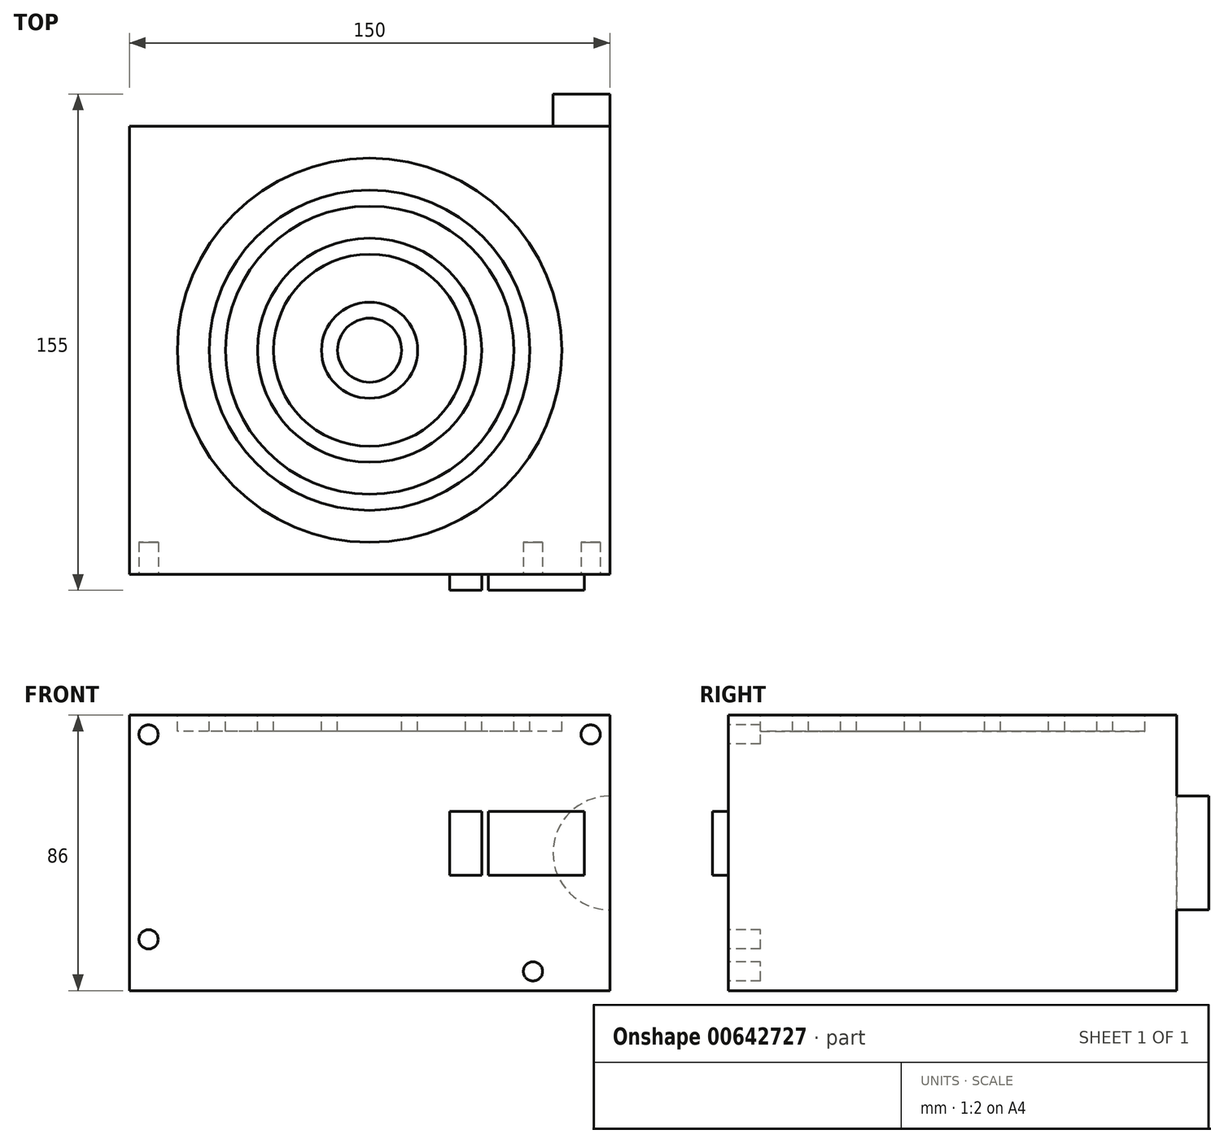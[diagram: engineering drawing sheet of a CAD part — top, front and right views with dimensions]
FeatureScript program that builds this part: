
annotation { "Feature Type Name" : "Feature", "Feature Type Description" : "" }
export const myFeature = defineFeature(function(context is Context, id is Id, definition is map)
    precondition{}
    {
        {
            var Q0;
            Q0=qCreatedBy(makeId("Top.planeOp"),FACE);
            var sketch = newSketch(context, id + "F0", { "sketchPlane" : qUnion([Q0])});
            skLineSegment(sketch, "E0.bottom", {"start": v(-67.65, 94.12) * mm, "end": v(82.35, 94.12) * mm});
            skLineSegment(sketch, "E0.top", {"start": v(-67.65, -45.88) * mm, "end": v(82.35, -45.88) * mm});
            skLineSegment(sketch, "E0.left", {"start": v(-67.65, 94.12) * mm, "end": v(-67.65, -45.88) * mm});
            skLineSegment(sketch, "E0.right", {"start": v(82.35, 94.12) * mm, "end": v(82.35, -45.88) * mm});
            skSolve(sketch);
        }
        {
            var Q0;
            Q0=makeQuery(id+"F0.imprint","IMPRINT",FACE,{"disambiguationData":[TD([[makeQuery(id+"F0.imprint","IMPRINT",EDGE,{"derivedFrom":sQuery(id+"F0.wireOp",EDGE,"E0.bottom")}),-1.0]])]});
            extrude(context, id + "F1", {"entities" : qUnion([Q0]), "depth" : 86 * mm, "offsetDistance" : 25 * mm});
        }
        {
            var Q0;
            Q0=makeQuery(id+"F1.opExtrude","SWEPT_FACE",FACE,{"disambiguationData":[OSD([sQuery(id+"F0.wireOp",EDGE,"E0.top")])]});
            var sketch = newSketch(context, id + "F2", { "sketchPlane" : qUnion([Q0])});
            skCircle(sketch, "E1", {"center": v(-61.65, 80) * mm, "radius": 3 * mm});
            skCircle(sketch, "E2", {"center": v(-61.65, 16) * mm, "radius": 3 * mm});
            skCircle(sketch, "E3", {"center": v(76.35, 80) * mm, "radius": 3 * mm});
            skCircle(sketch, "E4", {"center": v(58.35, 6) * mm, "radius": 3 * mm});
            skLineSegment(sketch, "E5.bottom", {"start": v(44.35, 56) * mm, "end": v(74.35, 56) * mm});
            skLineSegment(sketch, "E5.top", {"start": v(44.35, 36) * mm, "end": v(74.35, 36) * mm});
            skLineSegment(sketch, "E5.left", {"start": v(44.35, 56) * mm, "end": v(44.35, 36) * mm});
            skLineSegment(sketch, "E5.right", {"start": v(74.35, 56) * mm, "end": v(74.35, 36) * mm});
            skLineSegment(sketch, "E6.bottom", {"start": v(32.35, 56) * mm, "end": v(42.35, 56) * mm});
            skLineSegment(sketch, "E6.top", {"start": v(32.35, 36) * mm, "end": v(42.35, 36) * mm});
            skLineSegment(sketch, "E6.left", {"start": v(32.35, 56) * mm, "end": v(32.35, 36) * mm});
            skLineSegment(sketch, "E6.right", {"start": v(42.35, 56) * mm, "end": v(42.35, 36) * mm});
            skSolve(sketch);
        }
        {
            var Q0;
            Q0=makeQuery(id+"F2.imprint","IMPRINT",FACE,{"disambiguationData":[TD([[makeQuery(id+"F2.imprint","IMPRINT",EDGE,{"derivedFrom":sQuery(id+"F2.wireOp",EDGE,"E1")}),1.0]])]});
            var Q1;
            Q1=makeQuery(id+"F2.imprint","IMPRINT",FACE,{"disambiguationData":[TD([[makeQuery(id+"F2.imprint","IMPRINT",EDGE,{"derivedFrom":sQuery(id+"F2.wireOp",EDGE,"E2")}),1.0]])]});
            var Q2;
            Q2=makeQuery(id+"F2.imprint","IMPRINT",FACE,{"disambiguationData":[TD([[makeQuery(id+"F2.imprint","IMPRINT",EDGE,{"derivedFrom":sQuery(id+"F2.wireOp",EDGE,"E3")}),1.0]])]});
            var Q3;
            Q3=makeQuery(id+"F2.imprint","IMPRINT",FACE,{"disambiguationData":[TD([[makeQuery(id+"F2.imprint","IMPRINT",EDGE,{"derivedFrom":sQuery(id+"F2.wireOp",EDGE,"E4")}),1.0]])]});
            extrude(context, id + "F3", {"entities" : qUnion([Q0, Q1, Q2, Q3]), "operationType" : NewBodyOperationType.REMOVE, "oppositeDirection" : true, "depth" : 10 * mm, "offsetDistance" : 25 * mm});
        }
        {
            var Q0;
            Q0=makeQuery(id+"F2.imprint","IMPRINT",FACE,{"disambiguationData":[TD([[makeQuery(id+"F2.imprint","IMPRINT",EDGE,{"derivedFrom":sQuery(id+"F2.wireOp",EDGE,"E5.bottom")}),-1.0]])]});
            var Q1;
            Q1=makeQuery(id+"F2.imprint","IMPRINT",FACE,{"disambiguationData":[TD([[makeQuery(id+"F2.imprint","IMPRINT",EDGE,{"derivedFrom":sQuery(id+"F2.wireOp",EDGE,"E6.bottom")}),-1.0]])]});
            extrude(context, id + "F4", {"entities" : qUnion([Q0, Q1]), "operationType" : NewBodyOperationType.ADD, "depth" : 5 * mm, "offsetDistance" : 25 * mm});
        }
        {
            var Q0;
            Q0=makeQuery(id+"F1.opExtrude","CAP_FACE",FACE,{"disambiguationData":[OSD([sQuery(id+"F0.wireOp",EDGE,"E0.bottom"),sQuery(id+"F0.wireOp",EDGE,"E0.top"),sQuery(id+"F0.wireOp",EDGE,"E0.left"),sQuery(id+"F0.wireOp",EDGE,"E0.right")])],"isStart":false});
            var sketch = newSketch(context, id + "F5", { "sketchPlane" : qUnion([Q0])});
            skCircle(sketch, "E7", {"center": v(7.35, 24.12) * mm, "radius": 60 * mm});
            skPoint(sketch, "E7.centerSnap0", {"position": v(7.35, 94.12) * mm});
            skPoint(sketch, "E7.centerSnap1", {"position": v(82.35, 24.12) * mm});
            skCircle(sketch, "E8.0", {"center": v(7.35, 24.12) * mm, "radius": 50 * mm});
            skCircle(sketch, "E9.0", {"center": v(7.35, 24.12) * mm, "radius": 45 * mm});
            skCircle(sketch, "E10.0", {"center": v(7.35, 24.12) * mm, "radius": 35 * mm});
            skCircle(sketch, "E11.0", {"center": v(7.35, 24.12) * mm, "radius": 30 * mm});
            skCircle(sketch, "E12.0", {"center": v(7.35, 24.12) * mm, "radius": 15 * mm});
            skCircle(sketch, "E13.0", {"center": v(7.35, 24.12) * mm, "radius": 10 * mm});
            skSolve(sketch);
        }
        {
            var Q0;
            Q0=makeQuery(id+"F5.imprint","IMPRINT",FACE,{"disambiguationData":[TD([[makeQuery(id+"F5.imprint","IMPRINT",EDGE,{"derivedFrom":sQuery(id+"F5.wireOp",EDGE,"E7")}),1.0]])]});
            var Q1;
            Q1=makeQuery(id+"F5.imprint","IMPRINT",FACE,{"disambiguationData":[TD([[makeQuery(id+"F5.imprint","IMPRINT",EDGE,{"derivedFrom":sQuery(id+"F5.wireOp",EDGE,"E9.0")}),1.0]])]});
            var Q2;
            Q2=makeQuery(id+"F5.imprint","IMPRINT",FACE,{"disambiguationData":[TD([[makeQuery(id+"F5.imprint","IMPRINT",EDGE,{"derivedFrom":sQuery(id+"F5.wireOp",EDGE,"E11.0")}),1.0]])]});
            var Q3;
            Q3=makeQuery(id+"F5.imprint","IMPRINT",FACE,{"disambiguationData":[TD([[makeQuery(id+"F5.imprint","IMPRINT",EDGE,{"derivedFrom":sQuery(id+"F5.wireOp",EDGE,"E13.0")}),1.0]])]});
            extrude(context, id + "F6", {"entities" : qUnion([Q0, Q1, Q2, Q3]), "operationType" : NewBodyOperationType.REMOVE, "oppositeDirection" : true, "depth" : 5 * mm, "offsetDistance" : 25 * mm});
        }
        {
            var Q0;
            Q0=makeQuery(id+"F1.opExtrude","SWEPT_FACE",FACE,{"disambiguationData":[OSD([sQuery(id+"F0.wireOp",EDGE,"E0.bottom")])]});
            var sketch = newSketch(context, id + "F7", { "sketchPlane" : qUnion([Q0])});
            skCircle(sketch, "E14", {"center": v(-82.35, 43) * mm, "radius": 17.74 * mm});
            skSolve(sketch);
        }
        {
            var Q0;
            {var subQ0=sQuery(id+"F7.wireOp",EDGE,"E14");var subQ1=makeQuery(id+"F1.opExtrude","SWEPT_EDGE",EDGE,{"disambiguationData":[OSD([sQuery(id+"F0.wireOp",EDGE,"E0.bottom"),sQuery(id+"F0.wireOp",EDGE,"E0.right")])]});var subQ2=makeQuery(id+"F7.imprint","INTERSECT",VERTEX,{"disambiguationData":[OD(0.0)],"derivedFrom":[subQ1,subQ0]});Q0=makeQuery(id+"F7.imprint","IMPRINT",FACE,{"disambiguationData":[TD([[makeQuery(id+"F7.imprint","IMPRINT",EDGE,{"disambiguationData":[TD([[subQ2,-1.0]])],"derivedFrom":subQ0}),1.0]])]});}
            extrude(context, id + "F8", {"entities" : qUnion([Q0]), "operationType" : NewBodyOperationType.ADD, "depth" : 10 * mm, "offsetDistance" : 25 * mm});
        }
    });
